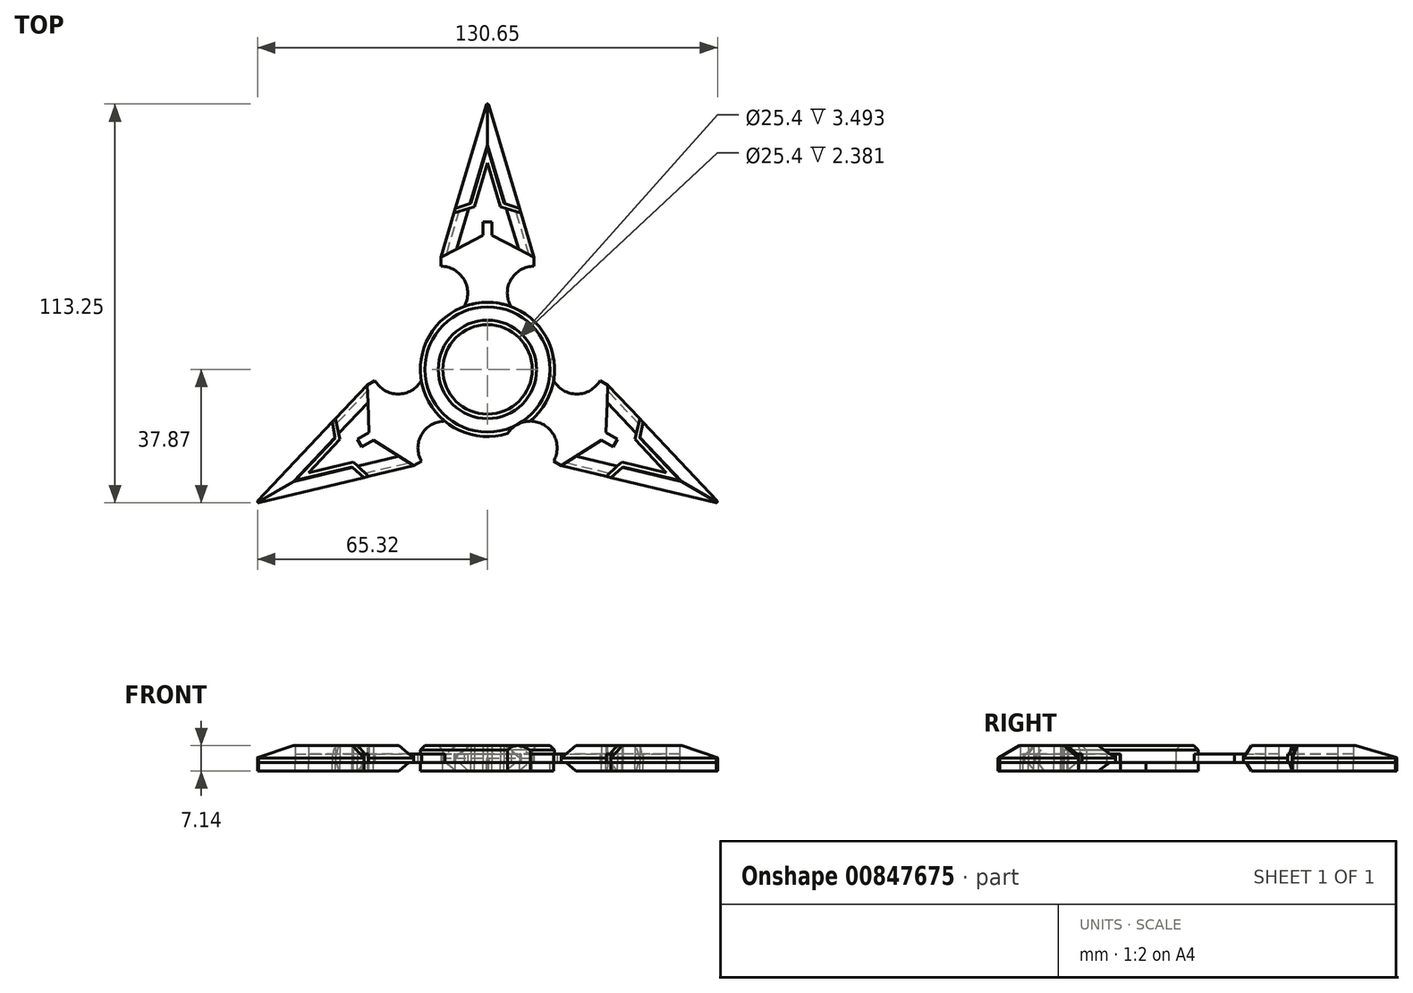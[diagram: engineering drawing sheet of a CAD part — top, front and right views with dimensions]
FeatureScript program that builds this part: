
annotation { "Feature Type Name" : "Feature", "Feature Type Description" : "" }
export const myFeature = defineFeature(function(context is Context, id is Id, definition is map)
    precondition{}
    {
        {
            var Q0;
            Q0=qCreatedBy(makeId("Top.planeOp"),FACE);
            var sketch = newSketch(context, id + "F0", { "sketchPlane" : qUnion([Q0])});
            skCircle(sketch, "E0", {"center": v(0, 0) * mm, "radius": 12.7 * mm});
            skCircle(sketch, "E1", {"center": v(0, 0) * mm, "radius": 19.05 * mm});
            skLineSegment(sketch, "E2", {"start": v(-0.28, 75.25) * mm, "end": v(-13.25, 31.83) * mm});
            skLineSegment(sketch, "E3", {"start": v(13.25, 31.83) * mm, "end": v(0.35, 75.03) * mm});
            skLineSegment(sketch, "E4", {"start": v(-13.25, 31.83) * mm, "end": v(-13.25, 29.3) * mm});
            skLineSegment(sketch, "E5", {"start": v(13.25, 31.83) * mm, "end": v(13.25, 29.3) * mm});
            skLineSegment(sketch, "E6", {"start": v(0, 0) * mm, "end": v(-4, 18.62) * mm});
            skPoint(sketch, "E7", {"position": v(-12.85, 14.06) * mm});
            skPoint(sketch, "E8", {"position": v(12.85, 14.06) * mm});
            skArc(sketch, "E9", {"start": v(-12.85, 14.06) * mm, "mid": v(-5.63, 21.87) * mm, "end": v(-13.25, 29.3) * mm});
            skArc(sketch, "E10", {"start": v(13.25, 29.3) * mm, "mid": v(5.63, 21.87) * mm, "end": v(12.85, 14.06) * mm});
            skPoint(sketch, "E11", {"position": v(0, 63.05) * mm});
            skPoint(sketch, "E12", {"position": v(-4.73, 47.22) * mm});
            skPoint(sketch, "E13", {"position": v(4.73, 47.22) * mm});
            skPoint(sketch, "E14", {"position": v(-9.1, 45.72) * mm});
            skPoint(sketch, "E15", {"position": v(9.12, 45.67) * mm});
            skLineSegment(sketch, "E16", {"start": v(-9.1, 45.72) * mm, "end": v(-4.73, 47.22) * mm});
            skLineSegment(sketch, "E17", {"start": v(0, 63.05) * mm, "end": v(-4.73, 47.22) * mm});
            skLineSegment(sketch, "E18", {"start": v(0, 63.05) * mm, "end": v(4.73, 47.22) * mm});
            skLineSegment(sketch, "E19", {"start": v(4.73, 47.22) * mm, "end": v(9.12, 45.67) * mm});
            skPoint(sketch, "E20", {"position": v(-9.48, 44.45) * mm});
            skPoint(sketch, "E21", {"position": v(9.48, 44.45) * mm});
            skPoint(sketch, "E22", {"position": v(0, 58.62) * mm});
            skLineSegment(sketch, "E23", {"start": v(-13.25, 31.83) * mm, "end": v(-1.27, 38.1) * mm});
            skLineSegment(sketch, "E24", {"start": v(-1.27, 38.1) * mm, "end": v(-1.27, 41.91) * mm});
            skLineSegment(sketch, "E25", {"start": v(-1.27, 41.91) * mm, "end": v(1.27, 41.91) * mm});
            skLineSegment(sketch, "E26", {"start": v(1.27, 41.91) * mm, "end": v(1.27, 38.1) * mm});
            skLineSegment(sketch, "E27", {"start": v(1.27, 38.1) * mm, "end": v(13.25, 31.83) * mm});
            skLineSegment(sketch, "E28", {"start": v(-9.48, 44.45) * mm, "end": v(-3.7, 46.2) * mm});
            skLineSegment(sketch, "E29", {"start": v(-3.7, 46.2) * mm, "end": v(0, 58.62) * mm});
            skLineSegment(sketch, "E30", {"start": v(0, 58.62) * mm, "end": v(3.7, 46.2) * mm});
            skLineSegment(sketch, "E31", {"start": v(3.7, 46.2) * mm, "end": v(9.48, 44.45) * mm});
            skPoint(sketch, "E32.1.0", {"position": v(-43.23, -14.01) * mm});
            skLineSegment(sketch, "E32.1.1", {"start": v(-65.03, -37.87) * mm, "end": v(-20.94, -27.39) * mm});
            skLineSegment(sketch, "E32.1.2", {"start": v(-33.63, -17.95) * mm, "end": v(-34.2, -4.44) * mm});
            skPoint(sketch, "E32.1.3", {"position": v(-54.6, -31.53) * mm});
            skLineSegment(sketch, "E32.1.4", {"start": v(-20.94, -27.39) * mm, "end": v(-32.36, -20.15) * mm});
            skLineSegment(sketch, "E32.1.5", {"start": v(-34.2, -4.44) * mm, "end": v(-65.28, -37.35) * mm});
            skPoint(sketch, "E32.1.6", {"position": v(-33.75, -30.44) * mm});
            skLineSegment(sketch, "E32.1.7", {"start": v(-54.6, -31.53) * mm, "end": v(-38.52, -27.7) * mm});
            skPoint(sketch, "E32.1.8", {"position": v(-38.52, -27.7) * mm});
            skLineSegment(sketch, "E32.1.9", {"start": v(-50.76, -29.3) * mm, "end": v(-41.86, -19.89) * mm});
            skPoint(sketch, "E32.1.10", {"position": v(-44.1, -14.94) * mm});
            skLineSegment(sketch, "E32.1.11", {"start": v(-54.6, -31.53) * mm, "end": v(-43.25, -19.51) * mm});
            skPoint(sketch, "E32.1.12", {"position": v(-50.76, -29.3) * mm});
            skPoint(sketch, "E32.1.13", {"position": v(-43.25, -19.51) * mm});
            skPoint(sketch, "E32.1.14", {"position": v(-35.04, -30.74) * mm});
            skLineSegment(sketch, "E32.1.15", {"start": v(-38.15, -26.3) * mm, "end": v(-50.76, -29.3) * mm});
            skLineSegment(sketch, "E32.1.16", {"start": v(-41.86, -19.89) * mm, "end": v(-43.23, -14.01) * mm});
            skLineSegment(sketch, "E32.1.17", {"start": v(-36.93, -19.86) * mm, "end": v(-33.63, -17.95) * mm});
            skLineSegment(sketch, "E32.1.18", {"start": v(-43.25, -19.51) * mm, "end": v(-44.1, -14.94) * mm});
            skLineSegment(sketch, "E32.1.19", {"start": v(-33.75, -30.44) * mm, "end": v(-38.15, -26.3) * mm});
            skLineSegment(sketch, "E32.1.20", {"start": v(-35.04, -30.74) * mm, "end": v(-38.52, -27.7) * mm});
            skLineSegment(sketch, "E32.1.21", {"start": v(-35.66, -22.05) * mm, "end": v(-36.93, -19.86) * mm});
            skLineSegment(sketch, "E32.1.22", {"start": v(-32.36, -20.15) * mm, "end": v(-35.66, -22.05) * mm});
            skLineSegment(sketch, "E32.1.23", {"start": v(-34.2, -4.44) * mm, "end": v(-32, -3.17) * mm});
            skLineSegment(sketch, "E32.1.24", {"start": v(-20.94, -27.39) * mm, "end": v(-18.74, -26.12) * mm});
            skArc(sketch, "E32.1.25", {"start": v(-32, -3.17) * mm, "mid": v(-21.75, -6.06) * mm, "end": v(-18.6, 4.1) * mm});
            skArc(sketch, "E32.1.26", {"start": v(-5.75, -18.16) * mm, "mid": v(-16.12, -15.81) * mm, "end": v(-18.74, -26.12) * mm});
            skPoint(sketch, "E32.2.0", {"position": v(33.75, -30.44) * mm});
            skLineSegment(sketch, "E32.2.1", {"start": v(65.31, -37.38) * mm, "end": v(34.2, -4.44) * mm});
            skLineSegment(sketch, "E32.2.2", {"start": v(32.36, -20.15) * mm, "end": v(20.94, -27.39) * mm});
            skPoint(sketch, "E32.2.3", {"position": v(54.6, -31.53) * mm});
            skLineSegment(sketch, "E32.2.4", {"start": v(34.2, -4.44) * mm, "end": v(33.63, -17.95) * mm});
            skLineSegment(sketch, "E32.2.5", {"start": v(20.94, -27.39) * mm, "end": v(64.98, -37.86) * mm});
            skPoint(sketch, "E32.2.6", {"position": v(43.23, -14.01) * mm});
            skLineSegment(sketch, "E32.2.7", {"start": v(54.6, -31.53) * mm, "end": v(43.25, -19.51) * mm});
            skPoint(sketch, "E32.2.8", {"position": v(43.25, -19.51) * mm});
            skLineSegment(sketch, "E32.2.9", {"start": v(50.76, -29.3) * mm, "end": v(38.15, -26.3) * mm});
            skPoint(sketch, "E32.2.10", {"position": v(35, -30.73) * mm});
            skLineSegment(sketch, "E32.2.11", {"start": v(54.6, -31.53) * mm, "end": v(38.52, -27.7) * mm});
            skPoint(sketch, "E32.2.12", {"position": v(50.76, -29.3) * mm});
            skPoint(sketch, "E32.2.13", {"position": v(38.52, -27.7) * mm});
            skPoint(sketch, "E32.2.14", {"position": v(44.15, -14.98) * mm});
            skLineSegment(sketch, "E32.2.15", {"start": v(41.86, -19.89) * mm, "end": v(50.76, -29.3) * mm});
            skLineSegment(sketch, "E32.2.16", {"start": v(38.15, -26.3) * mm, "end": v(33.75, -30.44) * mm});
            skLineSegment(sketch, "E32.2.17", {"start": v(35.66, -22.05) * mm, "end": v(32.36, -20.15) * mm});
            skLineSegment(sketch, "E32.2.18", {"start": v(38.52, -27.7) * mm, "end": v(35, -30.73) * mm});
            skLineSegment(sketch, "E32.2.19", {"start": v(43.23, -14.01) * mm, "end": v(41.86, -19.89) * mm});
            skLineSegment(sketch, "E32.2.20", {"start": v(44.15, -14.98) * mm, "end": v(43.25, -19.51) * mm});
            skLineSegment(sketch, "E32.2.21", {"start": v(36.93, -19.86) * mm, "end": v(35.66, -22.05) * mm});
            skLineSegment(sketch, "E32.2.22", {"start": v(33.63, -17.95) * mm, "end": v(36.93, -19.86) * mm});
            skLineSegment(sketch, "E32.2.23", {"start": v(20.94, -27.39) * mm, "end": v(18.74, -26.12) * mm});
            skLineSegment(sketch, "E32.2.24", {"start": v(34.2, -4.44) * mm, "end": v(32, -3.17) * mm});
            skArc(sketch, "E32.2.25", {"start": v(18.74, -26.12) * mm, "mid": v(16.12, -15.81) * mm, "end": v(5.75, -18.16) * mm});
            skArc(sketch, "E32.2.26", {"start": v(18.6, 4.1) * mm, "mid": v(21.75, -6.06) * mm, "end": v(32, -3.17) * mm});
            skCircle(sketch, "E33", {"center": v(228.68, 14.43) * mm, "radius": 12.7 * mm});
            skCircle(sketch, "E34", {"center": v(228.68, 14.43) * mm, "radius": 19.05 * mm});
            skLineSegment(sketch, "E35", {"start": v(228.68, 90.63) * mm, "end": v(215.43, 46.27) * mm});
            skLineSegment(sketch, "E36", {"start": v(241.93, 46.27) * mm, "end": v(228.68, 90.63) * mm});
            skLineSegment(sketch, "E37", {"start": v(215.43, 46.27) * mm, "end": v(215.43, 43.73) * mm});
            skLineSegment(sketch, "E38", {"start": v(241.93, 46.27) * mm, "end": v(241.93, 43.73) * mm});
            skPoint(sketch, "E39", {"position": v(215.83, 28.5) * mm});
            skPoint(sketch, "E40", {"position": v(241.53, 28.5) * mm});
            skArc(sketch, "E41", {"start": v(215.83, 28.5) * mm, "mid": v(223.05, 36.3) * mm, "end": v(215.43, 43.73) * mm});
            skArc(sketch, "E42", {"start": v(241.93, 43.73) * mm, "mid": v(234.3, 36.3) * mm, "end": v(241.53, 28.5) * mm});
            skPoint(sketch, "E43", {"position": v(228.68, 77.49) * mm});
            skPoint(sketch, "E44", {"position": v(223.95, 61.65) * mm});
            skPoint(sketch, "E45", {"position": v(233.4, 61.65) * mm});
            skPoint(sketch, "E46", {"position": v(219.58, 60.15) * mm});
            skPoint(sketch, "E47", {"position": v(237.8, 60.1) * mm});
            skLineSegment(sketch, "E48", {"start": v(219.58, 60.15) * mm, "end": v(223.95, 61.65) * mm});
            skLineSegment(sketch, "E49", {"start": v(228.68, 77.49) * mm, "end": v(223.95, 61.65) * mm});
            skLineSegment(sketch, "E50", {"start": v(228.68, 77.49) * mm, "end": v(233.4, 61.65) * mm});
            skLineSegment(sketch, "E51", {"start": v(233.4, 61.65) * mm, "end": v(237.8, 60.1) * mm});
            skPoint(sketch, "E52", {"position": v(219.2, 58.88) * mm});
            skPoint(sketch, "E53", {"position": v(238.16, 58.88) * mm});
            skPoint(sketch, "E54", {"position": v(228.68, 73.05) * mm});
            skLineSegment(sketch, "E55", {"start": v(215.43, 46.27) * mm, "end": v(227.4, 52.53) * mm});
            skLineSegment(sketch, "E56", {"start": v(227.4, 52.53) * mm, "end": v(227.4, 56.34) * mm});
            skLineSegment(sketch, "E57", {"start": v(227.4, 56.34) * mm, "end": v(229.95, 56.34) * mm});
            skLineSegment(sketch, "E58", {"start": v(229.95, 56.34) * mm, "end": v(229.95, 52.53) * mm});
            skLineSegment(sketch, "E59", {"start": v(229.95, 52.53) * mm, "end": v(241.93, 46.27) * mm});
            skLineSegment(sketch, "E60", {"start": v(219.2, 58.88) * mm, "end": v(224.97, 60.63) * mm});
            skLineSegment(sketch, "E61", {"start": v(224.97, 60.63) * mm, "end": v(228.68, 73.05) * mm});
            skLineSegment(sketch, "E62", {"start": v(228.68, 73.05) * mm, "end": v(232.39, 60.63) * mm});
            skLineSegment(sketch, "E63", {"start": v(232.39, 60.63) * mm, "end": v(238.16, 58.88) * mm});
            skPoint(sketch, "E64.1.0", {"position": v(185.44, 0.42) * mm});
            skLineSegment(sketch, "E64.1.1", {"start": v(162.69, -23.67) * mm, "end": v(207.73, -12.95) * mm});
            skLineSegment(sketch, "E64.1.2", {"start": v(195.05, -3.52) * mm, "end": v(194.49, 10) * mm});
            skPoint(sketch, "E64.1.3", {"position": v(174.07, -17.1) * mm});
            skLineSegment(sketch, "E64.1.4", {"start": v(207.73, -12.95) * mm, "end": v(196.32, -5.72) * mm});
            skLineSegment(sketch, "E64.1.5", {"start": v(194.49, 10) * mm, "end": v(162.69, -23.67) * mm});
            skPoint(sketch, "E64.1.6", {"position": v(194.92, -16) * mm});
            skLineSegment(sketch, "E64.1.7", {"start": v(174.07, -17.1) * mm, "end": v(190.15, -13.27) * mm});
            skPoint(sketch, "E64.1.8", {"position": v(190.15, -13.27) * mm});
            skLineSegment(sketch, "E64.1.9", {"start": v(177.92, -14.87) * mm, "end": v(186.82, -5.45) * mm});
            skPoint(sketch, "E64.1.10", {"position": v(184.57, -0.5) * mm});
            skLineSegment(sketch, "E64.1.11", {"start": v(174.07, -17.1) * mm, "end": v(185.42, -5.08) * mm});
            skPoint(sketch, "E64.1.12", {"position": v(177.92, -14.87) * mm});
            skPoint(sketch, "E64.1.13", {"position": v(185.42, -5.08) * mm});
            skPoint(sketch, "E64.1.14", {"position": v(193.63, -16.3) * mm});
            skLineSegment(sketch, "E64.1.15", {"start": v(190.52, -11.88) * mm, "end": v(177.92, -14.87) * mm});
            skLineSegment(sketch, "E64.1.16", {"start": v(186.82, -5.45) * mm, "end": v(185.44, 0.42) * mm});
            skLineSegment(sketch, "E64.1.17", {"start": v(191.75, -5.42) * mm, "end": v(195.05, -3.52) * mm});
            skLineSegment(sketch, "E64.1.18", {"start": v(185.42, -5.08) * mm, "end": v(184.57, -0.5) * mm});
            skLineSegment(sketch, "E64.1.19", {"start": v(194.92, -16) * mm, "end": v(190.52, -11.88) * mm});
            skLineSegment(sketch, "E64.1.20", {"start": v(193.63, -16.3) * mm, "end": v(190.15, -13.27) * mm});
            skLineSegment(sketch, "E64.1.21", {"start": v(193.02, -7.62) * mm, "end": v(191.75, -5.42) * mm});
            skLineSegment(sketch, "E64.1.22", {"start": v(196.32, -5.72) * mm, "end": v(193.02, -7.62) * mm});
            skLineSegment(sketch, "E64.1.23", {"start": v(194.49, 10) * mm, "end": v(196.69, 11.26) * mm});
            skLineSegment(sketch, "E64.1.24", {"start": v(207.73, -12.95) * mm, "end": v(209.93, -11.68) * mm});
            skArc(sketch, "E64.1.25", {"start": v(196.69, 11.26) * mm, "mid": v(206.92, 8.38) * mm, "end": v(210.07, 18.53) * mm});
            skArc(sketch, "E64.1.26", {"start": v(222.93, -3.73) * mm, "mid": v(212.55, -1.38) * mm, "end": v(209.93, -11.68) * mm});
            skPoint(sketch, "E64.2.0", {"position": v(262.43, -16) * mm});
            skLineSegment(sketch, "E64.2.1", {"start": v(294.67, -23.67) * mm, "end": v(262.87, 10) * mm});
            skLineSegment(sketch, "E64.2.2", {"start": v(261.04, -5.72) * mm, "end": v(249.62, -12.95) * mm});
            skPoint(sketch, "E64.2.3", {"position": v(283.28, -17.1) * mm});
            skLineSegment(sketch, "E64.2.4", {"start": v(262.87, 10) * mm, "end": v(262.3, -3.52) * mm});
            skLineSegment(sketch, "E64.2.5", {"start": v(249.62, -12.95) * mm, "end": v(294.67, -23.67) * mm});
            skPoint(sketch, "E64.2.6", {"position": v(271.91, 0.42) * mm});
            skLineSegment(sketch, "E64.2.7", {"start": v(283.28, -17.1) * mm, "end": v(271.93, -5.08) * mm});
            skPoint(sketch, "E64.2.8", {"position": v(271.93, -5.08) * mm});
            skLineSegment(sketch, "E64.2.9", {"start": v(279.44, -14.87) * mm, "end": v(266.83, -11.88) * mm});
            skPoint(sketch, "E64.2.10", {"position": v(263.67, -16.3) * mm});
            skLineSegment(sketch, "E64.2.11", {"start": v(283.28, -17.1) * mm, "end": v(267.2, -13.27) * mm});
            skPoint(sketch, "E64.2.12", {"position": v(279.44, -14.87) * mm});
            skPoint(sketch, "E64.2.13", {"position": v(267.2, -13.27) * mm});
            skPoint(sketch, "E64.2.14", {"position": v(272.82, -0.54) * mm});
            skLineSegment(sketch, "E64.2.15", {"start": v(270.54, -5.45) * mm, "end": v(279.44, -14.87) * mm});
            skLineSegment(sketch, "E64.2.16", {"start": v(266.83, -11.88) * mm, "end": v(262.43, -16) * mm});
            skLineSegment(sketch, "E64.2.17", {"start": v(264.34, -7.62) * mm, "end": v(261.04, -5.72) * mm});
            skLineSegment(sketch, "E64.2.18", {"start": v(267.2, -13.27) * mm, "end": v(263.67, -16.3) * mm});
            skLineSegment(sketch, "E64.2.19", {"start": v(271.91, 0.42) * mm, "end": v(270.54, -5.45) * mm});
            skLineSegment(sketch, "E64.2.20", {"start": v(272.82, -0.54) * mm, "end": v(271.93, -5.08) * mm});
            skLineSegment(sketch, "E64.2.21", {"start": v(265.6, -5.42) * mm, "end": v(264.34, -7.62) * mm});
            skLineSegment(sketch, "E64.2.22", {"start": v(262.3, -3.52) * mm, "end": v(265.6, -5.42) * mm});
            skLineSegment(sketch, "E64.2.23", {"start": v(249.62, -12.95) * mm, "end": v(247.42, -11.68) * mm});
            skLineSegment(sketch, "E64.2.24", {"start": v(262.87, 10) * mm, "end": v(260.67, 11.26) * mm});
            skArc(sketch, "E64.2.25", {"start": v(247.42, -11.68) * mm, "mid": v(244.8, -1.38) * mm, "end": v(234.43, -3.73) * mm});
            skArc(sketch, "E64.2.26", {"start": v(247.28, 18.53) * mm, "mid": v(250.43, 8.38) * mm, "end": v(260.67, 11.26) * mm});
            skArc(sketch, "E65", {"start": v(0.26, 75.26) * mm, "mid": v(-0.01, 75.38) * mm, "end": v(-0.28, 75.25) * mm});
            skPoint(sketch, "E66.orphan", {"position": v(0, 76.2) * mm});
            skArc(sketch, "E67.1.0", {"start": v(-65.28, -37.35) * mm, "mid": v(-65.29, -37.67) * mm, "end": v(-65.03, -37.87) * mm});
            skArc(sketch, "E67.2.0", {"start": v(64.98, -37.86) * mm, "mid": v(65.27, -37.7) * mm, "end": v(65.31, -37.38) * mm});
            skPoint(sketch, "E68.orphan", {"position": v(66, -38.1) * mm});
            skPoint(sketch, "E69.orphan", {"position": v(-66, -38.1) * mm});
            skPoint(sketch, "E70.orphan", {"position": v(-65.15, -37.21) * mm});
            skPoint(sketch, "E71.orphan", {"position": v(-64.75, -37.8) * mm});
            skPoint(sketch, "E72.orphan", {"position": v(65.11, -37.17) * mm});
            skPoint(sketch, "E73.orphan", {"position": v(64.8, -37.82) * mm});
            skPoint(sketch, "E74.orphan", {"position": v(-0.37, 74.98) * mm});
            skLineSegment(sketch, "E75", {"start": v(0.35, 75.03) * mm, "end": v(0.26, 75.26) * mm});
            skSolve(sketch);
        }
        {
            var Q0;
            Q0=makeQuery(id+"F0.imprint","IMPRINT",FACE,{"disambiguationData":[TD([[makeQuery(id+"F0.imprint","IMPRINT",EDGE,{"derivedFrom":sQuery(id+"F0.wireOp",EDGE,"E32.2.2")}),-1.0]])]});
            var Q1;
            Q1=makeQuery(id+"F0.imprint","IMPRINT",FACE,{"disambiguationData":[TD([[makeQuery(id+"F0.imprint","IMPRINT",EDGE,{"derivedFrom":sQuery(id+"F0.wireOp",EDGE,"E32.1.2")}),-1.0]])]});
            var Q2;
            {var subQ5=sQuery(id+"F0.wireOp",EDGE,"E4");Q2=makeQuery(id+"F0.imprint","IMPRINT",FACE,{"disambiguationData":[TD([[makeQuery(id+"F0.imprint","IMPRINT",EDGE,{"derivedFrom":subQ5}),1.0]])]});}
            var Q3;
            {var subQ1=sQuery(id+"F0.wireOp",EDGE,"E16");Q3=makeQuery(id+"F0.imprint","IMPRINT",FACE,{"disambiguationData":[TD([[makeQuery(id+"F0.imprint","IMPRINT",EDGE,{"derivedFrom":subQ1}),-1.0]])]});}
            var Q4;
            Q4=makeQuery(id+"F0.imprint","IMPRINT",FACE,{"disambiguationData":[TD([[makeQuery(id+"F0.imprint","IMPRINT",EDGE,{"derivedFrom":sQuery(id+"F0.wireOp",EDGE,"E32.2.7")}),1.0]])]});
            var Q5;
            Q5=makeQuery(id+"F0.imprint","IMPRINT",FACE,{"disambiguationData":[TD([[makeQuery(id+"F0.imprint","IMPRINT",EDGE,{"derivedFrom":sQuery(id+"F0.wireOp",EDGE,"E32.1.7")}),1.0]])]});
            extrude(context, id + "F1", {"entities" : qUnion([Q0, Q1, Q2, Q3, Q4, Q5]), "depth" : 2.38 * mm, "offsetDistance" : 25.4 * mm});
        }
        {
            var Q0;
            {var subQ2=sQuery(id+"F0.wireOp",EDGE,"E23");Q0=makeQuery(id+"F0.imprint","IMPRINT",FACE,{"disambiguationData":[TD([[makeQuery(id+"F0.imprint","IMPRINT",EDGE,{"derivedFrom":subQ2}),1.0]])]});}
            var Q1;
            {var subQ0=sQuery(id+"F0.wireOp",EDGE,"E16");Q1=makeQuery(id+"F0.imprint","IMPRINT",FACE,{"disambiguationData":[TD([[makeQuery(id+"F0.imprint","IMPRINT",EDGE,{"derivedFrom":subQ0}),1.0]])]});}
            var Q2;
            {var subQ4=sQuery(id+"F0.wireOp",EDGE,"E32.2.2");Q2=makeQuery(id+"F0.imprint","IMPRINT",FACE,{"disambiguationData":[TD([[makeQuery(id+"F0.imprint","IMPRINT",EDGE,{"derivedFrom":subQ4}),1.0]])]});}
            var Q3;
            Q3=makeQuery(id+"F0.imprint","IMPRINT",FACE,{"disambiguationData":[TD([[makeQuery(id+"F0.imprint","IMPRINT",EDGE,{"derivedFrom":sQuery(id+"F0.wireOp",EDGE,"E32.2.7")}),-1.0]])]});
            var Q4;
            Q4=makeQuery(id+"F0.imprint","IMPRINT",FACE,{"disambiguationData":[TD([[makeQuery(id+"F0.imprint","IMPRINT",EDGE,{"derivedFrom":sQuery(id+"F0.wireOp",EDGE,"E32.1.7")}),-1.0]])]});
            var Q5;
            {var subQ4=sQuery(id+"F0.wireOp",EDGE,"E32.1.2");Q5=makeQuery(id+"F0.imprint","IMPRINT",FACE,{"disambiguationData":[TD([[makeQuery(id+"F0.imprint","IMPRINT",EDGE,{"derivedFrom":subQ4}),1.0]])]});}
            var Q6;
            Q6=makeQuery(id+"F0.imprint","IMPRINT",FACE,{"disambiguationData":[TD([[makeQuery(id+"F0.imprint","IMPRINT",EDGE,{"derivedFrom":sQuery(id+"F0.wireOp",EDGE,"E0")}),-1.0]])]});
            var Q7;
            {var subQ0=sQuery(id+"F0.wireOp",EDGE,"E32.2.26");var subQ1=sQuery(id+"F0.wireOp",EDGE,"E1");var subQ2=makeQuery(id+"F0.imprint","INTERSECT",VERTEX,{"disambiguationData":[OD(0.0)],"derivedFrom":[subQ1,subQ0]});Q7=makeQuery(id+"F0.imprint","IMPRINT",FACE,{"disambiguationData":[TD([[makeQuery(id+"F0.imprint","IMPRINT",EDGE,{"disambiguationData":[TD([[subQ2,1.0]])],"derivedFrom":subQ1}),1.0]])]});}
            var Q8;
            {var subQ0=sQuery(id+"F0.wireOp",EDGE,"E32.2.25");var subQ1=sQuery(id+"F0.wireOp",EDGE,"E1");var subQ2=makeQuery(id+"F0.imprint","INTERSECT",VERTEX,{"disambiguationData":[OD(0.0)],"derivedFrom":[subQ1,subQ0]});Q8=makeQuery(id+"F0.imprint","IMPRINT",FACE,{"disambiguationData":[TD([[makeQuery(id+"F0.imprint","IMPRINT",EDGE,{"disambiguationData":[TD([[subQ2,-1.0]])],"derivedFrom":subQ1}),1.0]])]});}
            var Q9;
            {var subQ0=sQuery(id+"F0.wireOp",EDGE,"E32.1.26");var subQ1=sQuery(id+"F0.wireOp",EDGE,"E1");var subQ2=makeQuery(id+"F0.imprint","INTERSECT",VERTEX,{"disambiguationData":[OD(0.0)],"derivedFrom":[subQ1,subQ0]});Q9=makeQuery(id+"F0.imprint","IMPRINT",FACE,{"disambiguationData":[TD([[makeQuery(id+"F0.imprint","IMPRINT",EDGE,{"disambiguationData":[TD([[subQ2,1.0]])],"derivedFrom":subQ1}),1.0]])]});}
            var Q10;
            {var subQ0=sQuery(id+"F0.wireOp",EDGE,"E32.1.25");var subQ1=sQuery(id+"F0.wireOp",EDGE,"E1");var subQ2=makeQuery(id+"F0.imprint","INTERSECT",VERTEX,{"disambiguationData":[OD(0.0)],"derivedFrom":[subQ1,subQ0]});Q10=makeQuery(id+"F0.imprint","IMPRINT",FACE,{"disambiguationData":[TD([[makeQuery(id+"F0.imprint","IMPRINT",EDGE,{"disambiguationData":[TD([[subQ2,-1.0]])],"derivedFrom":subQ1}),1.0]])]});}
            var Q11;
            {var subQ0=sQuery(id+"F0.wireOp",EDGE,"E9");var subQ1=sQuery(id+"F0.wireOp",EDGE,"E1");var subQ2=makeQuery(id+"F0.imprint","INTERSECT",VERTEX,{"disambiguationData":[OD(0.0)],"derivedFrom":[subQ1,subQ0]});Q11=makeQuery(id+"F0.imprint","IMPRINT",FACE,{"disambiguationData":[TD([[makeQuery(id+"F0.imprint","IMPRINT",EDGE,{"disambiguationData":[TD([[subQ2,1.0]])],"derivedFrom":subQ1}),1.0]])]});}
            var Q12;
            {var subQ0=sQuery(id+"F0.wireOp",EDGE,"E10");var subQ1=sQuery(id+"F0.wireOp",EDGE,"E1");var subQ2=makeQuery(id+"F0.imprint","INTERSECT",VERTEX,{"disambiguationData":[OD(0.0)],"derivedFrom":[subQ1,subQ0]});Q12=makeQuery(id+"F0.imprint","IMPRINT",FACE,{"disambiguationData":[TD([[makeQuery(id+"F0.imprint","IMPRINT",EDGE,{"disambiguationData":[TD([[subQ2,-1.0]])],"derivedFrom":subQ1}),1.0]])]});}
            extrude(context, id + "F2", {"entities" : qUnion([Q0, Q1, Q2, Q3, Q4, Q5, Q6, Q7, Q8, Q9, Q10, Q11, Q12]), "depth" : 4.76 * mm, "offsetDistance" : 25.4 * mm});
        }
        {
            var Q0;
            Q0=makeQuery(id+"F0.imprint","IMPRINT",FACE,{"disambiguationData":[TD([[makeQuery(id+"F0.imprint","IMPRINT",EDGE,{"derivedFrom":sQuery(id+"F0.wireOp",EDGE,"E0")}),-1.0]])]});
            var Q1;
            {var subQ0=sQuery(id+"F0.wireOp",EDGE,"E32.2.25");var subQ1=sQuery(id+"F0.wireOp",EDGE,"E1");var subQ2=makeQuery(id+"F0.imprint","INTERSECT",VERTEX,{"disambiguationData":[OD(0.0)],"derivedFrom":[subQ1,subQ0]});Q1=makeQuery(id+"F0.imprint","IMPRINT",FACE,{"disambiguationData":[TD([[makeQuery(id+"F0.imprint","IMPRINT",EDGE,{"disambiguationData":[TD([[subQ2,-1.0]])],"derivedFrom":subQ1}),1.0]])]});}
            var Q2;
            {var subQ0=sQuery(id+"F0.wireOp",EDGE,"E32.1.26");var subQ1=sQuery(id+"F0.wireOp",EDGE,"E1");var subQ2=makeQuery(id+"F0.imprint","INTERSECT",VERTEX,{"disambiguationData":[OD(0.0)],"derivedFrom":[subQ1,subQ0]});Q2=makeQuery(id+"F0.imprint","IMPRINT",FACE,{"disambiguationData":[TD([[makeQuery(id+"F0.imprint","IMPRINT",EDGE,{"disambiguationData":[TD([[subQ2,1.0]])],"derivedFrom":subQ1}),1.0]])]});}
            var Q3;
            {var subQ0=sQuery(id+"F0.wireOp",EDGE,"E32.1.25");var subQ1=sQuery(id+"F0.wireOp",EDGE,"E1");var subQ2=makeQuery(id+"F0.imprint","INTERSECT",VERTEX,{"disambiguationData":[OD(0.0)],"derivedFrom":[subQ1,subQ0]});Q3=makeQuery(id+"F0.imprint","IMPRINT",FACE,{"disambiguationData":[TD([[makeQuery(id+"F0.imprint","IMPRINT",EDGE,{"disambiguationData":[TD([[subQ2,-1.0]])],"derivedFrom":subQ1}),1.0]])]});}
            var Q4;
            {var subQ0=sQuery(id+"F0.wireOp",EDGE,"E9");var subQ1=sQuery(id+"F0.wireOp",EDGE,"E1");var subQ2=makeQuery(id+"F0.imprint","INTERSECT",VERTEX,{"disambiguationData":[OD(0.0)],"derivedFrom":[subQ1,subQ0]});Q4=makeQuery(id+"F0.imprint","IMPRINT",FACE,{"disambiguationData":[TD([[makeQuery(id+"F0.imprint","IMPRINT",EDGE,{"disambiguationData":[TD([[subQ2,1.0]])],"derivedFrom":subQ1}),1.0]])]});}
            var Q5;
            {var subQ0=sQuery(id+"F0.wireOp",EDGE,"E10");var subQ1=sQuery(id+"F0.wireOp",EDGE,"E1");var subQ2=makeQuery(id+"F0.imprint","INTERSECT",VERTEX,{"disambiguationData":[OD(0.0)],"derivedFrom":[subQ1,subQ0]});Q5=makeQuery(id+"F0.imprint","IMPRINT",FACE,{"disambiguationData":[TD([[makeQuery(id+"F0.imprint","IMPRINT",EDGE,{"disambiguationData":[TD([[subQ2,-1.0]])],"derivedFrom":subQ1}),1.0]])]});}
            var Q6;
            {var subQ4=sQuery(id+"F0.wireOp",EDGE,"E32.2.2");Q6=makeQuery(id+"F0.imprint","IMPRINT",FACE,{"disambiguationData":[TD([[makeQuery(id+"F0.imprint","IMPRINT",EDGE,{"derivedFrom":subQ4}),1.0]])]});}
            var Q7;
            Q7=makeQuery(id+"F0.imprint","IMPRINT",FACE,{"disambiguationData":[TD([[makeQuery(id+"F0.imprint","IMPRINT",EDGE,{"derivedFrom":sQuery(id+"F0.wireOp",EDGE,"E32.2.7")}),-1.0]])]});
            var Q8;
            {var subQ4=sQuery(id+"F0.wireOp",EDGE,"E32.1.2");Q8=makeQuery(id+"F0.imprint","IMPRINT",FACE,{"disambiguationData":[TD([[makeQuery(id+"F0.imprint","IMPRINT",EDGE,{"derivedFrom":subQ4}),1.0]])]});}
            var Q9;
            Q9=makeQuery(id+"F0.imprint","IMPRINT",FACE,{"disambiguationData":[TD([[makeQuery(id+"F0.imprint","IMPRINT",EDGE,{"derivedFrom":sQuery(id+"F0.wireOp",EDGE,"E32.1.7")}),-1.0]])]});
            var Q10;
            {var subQ2=sQuery(id+"F0.wireOp",EDGE,"E23");Q10=makeQuery(id+"F0.imprint","IMPRINT",FACE,{"disambiguationData":[TD([[makeQuery(id+"F0.imprint","IMPRINT",EDGE,{"derivedFrom":subQ2}),1.0]])]});}
            var Q11;
            {var subQ0=sQuery(id+"F0.wireOp",EDGE,"E16");Q11=makeQuery(id+"F0.imprint","IMPRINT",FACE,{"disambiguationData":[TD([[makeQuery(id+"F0.imprint","IMPRINT",EDGE,{"derivedFrom":subQ0}),1.0]])]});}
            extrude(context, id + "F3", {"entities" : qUnion([Q0, Q1, Q2, Q3, Q4, Q5, Q6, Q7, Q8, Q9, Q10, Q11]), "oppositeDirection" : true, "depth" : 2.38 * mm, "offsetDistance" : 25.4 * mm});
        }
        {
            var Q0;
            {var subQ0=sQuery(id+"F0.wireOp",EDGE,"E32.1.1");Q0=makeQuery(id+"F2.opExtrude","CAP_EDGE",EDGE,{"disambiguationData":[OSD([subQ0]),TDD([makeQuery(id+"F0.imprint","IMPRINT",EDGE,{"disambiguationData":[TD([[makeQuery(id+"F0.imprint","INTERSECT",VERTEX,{"derivedFrom":[subQ0,sQuery(id+"F0.wireOp",EDGE,"E32.1.5")]}),-1.0]])],"derivedFrom":subQ0})])],"isStart":false});}
            var Q1;
            {var subQ0=sQuery(id+"F0.wireOp",EDGE,"E32.1.1");Q1=makeQuery(id+"F3.opExtrude","CAP_EDGE",EDGE,{"disambiguationData":[OSD([subQ0]),TDD([makeQuery(id+"F0.imprint","IMPRINT",EDGE,{"disambiguationData":[TD([[makeQuery(id+"F0.imprint","INTERSECT",VERTEX,{"derivedFrom":[subQ0,sQuery(id+"F0.wireOp",EDGE,"E32.1.5")]}),-1.0]])],"derivedFrom":subQ0})])],"isStart":false});}
            var Q2;
            {var subQ0=sQuery(id+"F0.wireOp",EDGE,"E32.1.5");Q2=makeQuery(id+"F2.opExtrude","CAP_EDGE",EDGE,{"disambiguationData":[OSD([subQ0]),TDD([makeQuery(id+"F0.imprint","IMPRINT",EDGE,{"disambiguationData":[TD([[makeQuery(id+"F0.imprint","INTERSECT",VERTEX,{"derivedFrom":[sQuery(id+"F0.wireOp",EDGE,"E32.1.1"),subQ0]}),1.0]])],"derivedFrom":subQ0})])],"isStart":false});}
            var Q3;
            {var subQ0=sQuery(id+"F0.wireOp",EDGE,"E32.1.5");Q3=makeQuery(id+"F3.opExtrude","CAP_EDGE",EDGE,{"disambiguationData":[OSD([subQ0]),TDD([makeQuery(id+"F0.imprint","IMPRINT",EDGE,{"disambiguationData":[TD([[makeQuery(id+"F0.imprint","INTERSECT",VERTEX,{"derivedFrom":[sQuery(id+"F0.wireOp",EDGE,"E32.1.1"),subQ0]}),1.0]])],"derivedFrom":subQ0})])],"isStart":false});}
            var Q4;
            {var subQ0=sQuery(id+"F0.wireOp",EDGE,"E32.2.5");Q4=makeQuery(id+"F2.opExtrude","CAP_EDGE",EDGE,{"disambiguationData":[OSD([subQ0]),TDD([makeQuery(id+"F0.imprint","IMPRINT",EDGE,{"disambiguationData":[TD([[makeQuery(id+"F0.imprint","INTERSECT",VERTEX,{"derivedFrom":[sQuery(id+"F0.wireOp",EDGE,"E32.2.1"),subQ0]}),1.0]])],"derivedFrom":subQ0})])],"isStart":false});}
            var Q5;
            {var subQ0=sQuery(id+"F0.wireOp",EDGE,"E32.2.5");Q5=makeQuery(id+"F3.opExtrude","CAP_EDGE",EDGE,{"disambiguationData":[OSD([subQ0]),TDD([makeQuery(id+"F0.imprint","IMPRINT",EDGE,{"disambiguationData":[TD([[makeQuery(id+"F0.imprint","INTERSECT",VERTEX,{"derivedFrom":[sQuery(id+"F0.wireOp",EDGE,"E32.2.1"),subQ0]}),1.0]])],"derivedFrom":subQ0})])],"isStart":false});}
            var Q6;
            {var subQ0=sQuery(id+"F0.wireOp",EDGE,"E32.2.1");Q6=makeQuery(id+"F2.opExtrude","CAP_EDGE",EDGE,{"disambiguationData":[OSD([subQ0]),TDD([makeQuery(id+"F0.imprint","IMPRINT",EDGE,{"disambiguationData":[TD([[makeQuery(id+"F0.imprint","INTERSECT",VERTEX,{"derivedFrom":[subQ0,sQuery(id+"F0.wireOp",EDGE,"E32.2.5")]}),-1.0]])],"derivedFrom":subQ0})])],"isStart":false});}
            var Q7;
            {var subQ0=sQuery(id+"F0.wireOp",EDGE,"E32.2.1");Q7=makeQuery(id+"F3.opExtrude","CAP_EDGE",EDGE,{"disambiguationData":[OSD([subQ0]),TDD([makeQuery(id+"F0.imprint","IMPRINT",EDGE,{"disambiguationData":[TD([[makeQuery(id+"F0.imprint","INTERSECT",VERTEX,{"derivedFrom":[subQ0,sQuery(id+"F0.wireOp",EDGE,"E32.2.5")]}),-1.0]])],"derivedFrom":subQ0})])],"isStart":false});}
            var Q8;
            {var subQ0=sQuery(id+"F0.wireOp",EDGE,"E3");Q8=makeQuery(id+"F2.opExtrude","CAP_EDGE",EDGE,{"disambiguationData":[OSD([subQ0]),TDD([makeQuery(id+"F0.imprint","IMPRINT",EDGE,{"disambiguationData":[TD([[makeQuery(id+"F0.imprint","INTERSECT",VERTEX,{"derivedFrom":[sQuery(id+"F0.wireOp",EDGE,"E2"),subQ0]}),1.0]])],"derivedFrom":subQ0})])],"isStart":false});}
            var Q9;
            {var subQ0=sQuery(id+"F0.wireOp",EDGE,"E3");Q9=makeQuery(id+"F3.opExtrude","CAP_EDGE",EDGE,{"disambiguationData":[OSD([subQ0]),TDD([makeQuery(id+"F0.imprint","IMPRINT",EDGE,{"disambiguationData":[TD([[makeQuery(id+"F0.imprint","INTERSECT",VERTEX,{"derivedFrom":[sQuery(id+"F0.wireOp",EDGE,"E2"),subQ0]}),1.0]])],"derivedFrom":subQ0})])],"isStart":false});}
            var Q10;
            {var subQ0=sQuery(id+"F0.wireOp",EDGE,"E2");Q10=makeQuery(id+"F3.opExtrude","CAP_EDGE",EDGE,{"disambiguationData":[OSD([subQ0]),TDD([makeQuery(id+"F0.imprint","IMPRINT",EDGE,{"disambiguationData":[TD([[makeQuery(id+"F0.imprint","INTERSECT",VERTEX,{"derivedFrom":[subQ0,sQuery(id+"F0.wireOp",EDGE,"E3")]}),-1.0]])],"derivedFrom":subQ0})])],"isStart":false});}
            var Q11;
            {var subQ0=sQuery(id+"F0.wireOp",EDGE,"E2");Q11=makeQuery(id+"F2.opExtrude","CAP_EDGE",EDGE,{"disambiguationData":[OSD([subQ0]),TDD([makeQuery(id+"F0.imprint","IMPRINT",EDGE,{"disambiguationData":[TD([[makeQuery(id+"F0.imprint","INTERSECT",VERTEX,{"derivedFrom":[subQ0,sQuery(id+"F0.wireOp",EDGE,"E3")]}),-1.0]])],"derivedFrom":subQ0})])],"isStart":false});}
            chamfer(context, id + "F4", {"entities" : qUnion([Q0, Q1, Q2, Q3, Q4, Q5, Q6, Q7, Q8, Q9, Q10, Q11]), "width" : 3.57 * mm, "tangentPropagation" : true});
        }
        {
            var Q0;
            Q0=makeQuery(id+"F2.opExtrude","CAP_EDGE",EDGE,{"disambiguationData":[OSD([sQuery(id+"F0.wireOp",EDGE,"E1")])],"isStart":false});
            var Q1;
            Q1=makeQuery(id+"F2.opExtrude","CAP_EDGE",EDGE,{"disambiguationData":[OSD([sQuery(id+"F0.wireOp",EDGE,"E0")])],"isStart":false});
            chamfer(context, id + "F5", {"entities" : qUnion([Q0, Q1]), "width" : 1.27 * mm, "tangentPropagation" : true});
        }
    });
